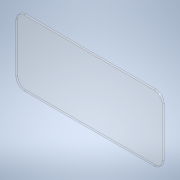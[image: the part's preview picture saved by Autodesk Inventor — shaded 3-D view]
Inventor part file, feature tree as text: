
AUTODESK INVENTOR PART (.ipt)
format: ipt  version: 2020 (Build 240168000, 168)  size: 104,960 bytes
history: native  units: in
note: dims shown in document units (in); Inventor stores cm internally (conversion verified against a paired STEP export)
features: extrude x1, sketch x1
ambient origin geometry x8: Origin, YZ Plane, XZ Plane, XY Plane, X Axis, Y Axis, Z Axis, Center Point
bodies: Solid1 (feature_tree)
feature tree (2):
  extrude  "Extrusion1"  Depth=8.061in
  sketch  "Sketch1"  dims[d0=17.931in d1=8.061in d2=1.0in d3=0.227in d4=0.0in]
